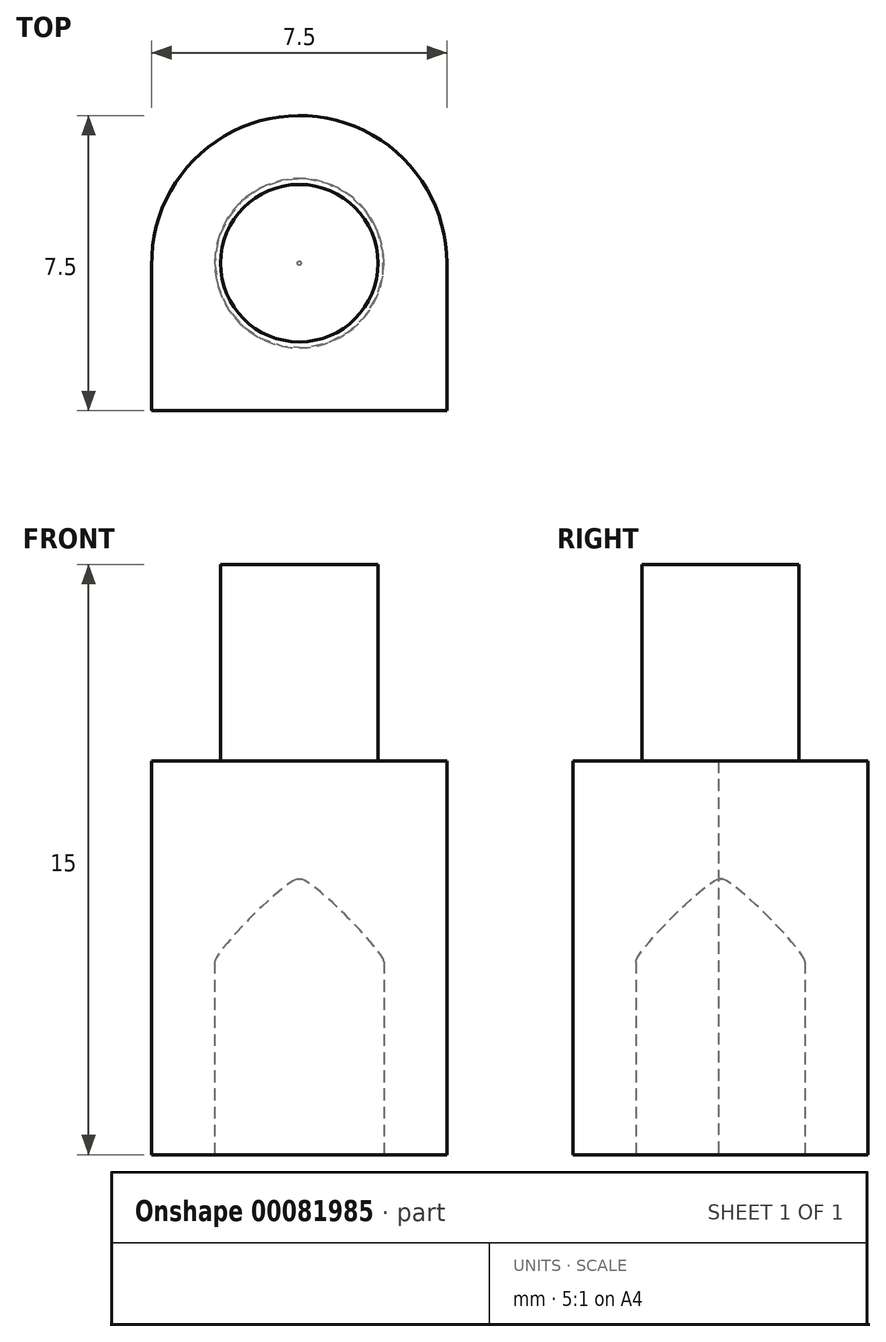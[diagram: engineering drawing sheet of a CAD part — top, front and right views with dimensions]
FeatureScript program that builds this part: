
annotation { "Feature Type Name" : "Feature", "Feature Type Description" : "" }
export const myFeature = defineFeature(function(context is Context, id is Id, definition is map)
    precondition{}
    {
        {
            var Q0;
            Q0=qCreatedBy(makeId("Top.planeOp"),FACE);
            var sketch = newSketch(context, id + "F0", { "sketchPlane" : qUnion([Q0])});
            skArc(sketch, "E0", {"start": v(3.75, 0) * mm, "mid": v(-0.03, 3.75) * mm, "end": v(-3.75, -0.06) * mm});
            skLineSegment(sketch, "E1", {"start": v(3.75, 0) * mm, "end": v(3.75, -3.75) * mm});
            skLineSegment(sketch, "E2", {"start": v(3.75, -3.75) * mm, "end": v(-3.75, -3.75) * mm});
            skLineSegment(sketch, "E3", {"start": v(-3.75, -3.75) * mm, "end": v(-3.75, 0) * mm});
            skSolve(sketch);
        }
        {
            var Q0;
            Q0 = qSketchRegion(id + "F0", true);
            extrude(context, id + "F1", {"entities" : qUnion([Q0]), "depth" : 10 * mm});
        }
        {
            var Q0;
            Q0=makeQuery(id+"F1.opExtrude","CAP_FACE",FACE,{"disambiguationData":[OSD([sQuery(id+"F0.wireOp",EDGE,"E0"),sQuery(id+"F0.wireOp",EDGE,"E1"),sQuery(id+"F0.wireOp",EDGE,"E2"),sQuery(id+"F0.wireOp",EDGE,"E3")])],"isStart":true});
            var sketch = newSketch(context, id + "F2", { "sketchPlane" : qUnion([Q0])});
            skCircle(sketch, "E4", {"center": v(0, 0) * mm, "radius": 2.15 * mm});
            skSolve(sketch);
        }
        {
            var Q0;
            Q0 = qSketchRegion(id + "F2", true);
            extrude(context, id + "F3", {"entities" : qUnion([Q0]), "operationType" : NewBodyOperationType.REMOVE, "oppositeDirection" : true, "depth" : 7 * mm});
        }
        {
            var Q0;
            Q0=makeQuery(id+"F3.boolean.opBoolean","COPY",FACE,{"derivedFrom":makeQuery(id+"F3.opExtrude","CAP_FACE",FACE,{"disambiguationData":[OSD([sQuery(id+"F2.wireOp",EDGE,"E4")])],"isStart":false})});
            fillet(context, id + "F4", {"entities" : qUnion([Q0]), "radius" : 2.1 * mm, "tangentPropagation" : true, "rho" : 0.1, "crossSection" : FilletCrossSection.CONIC, "allowEdgeOverflow" : false});
        }
        {
            var Q0;
            Q0=makeQuery(id+"F1.opExtrude","CAP_FACE",FACE,{"disambiguationData":[OSD([sQuery(id+"F0.wireOp",EDGE,"E0"),sQuery(id+"F0.wireOp",EDGE,"E1"),sQuery(id+"F0.wireOp",EDGE,"E2"),sQuery(id+"F0.wireOp",EDGE,"E3")])],"isStart":false});
            var sketch = newSketch(context, id + "F5", { "sketchPlane" : qUnion([Q0])});
            skCircle(sketch, "E5", {"center": v(0, 0) * mm, "radius": 2 * mm});
            skSolve(sketch);
        }
        {
            var Q0;
            Q0 = qSketchRegion(id + "F5", true);
            extrude(context, id + "F6", {"entities" : qUnion([Q0]), "operationType" : NewBodyOperationType.ADD, "depth" : 5 * mm});
        }
    });
